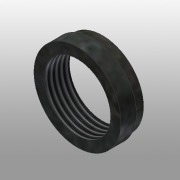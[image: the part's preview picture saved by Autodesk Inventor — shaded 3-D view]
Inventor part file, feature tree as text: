
AUTODESK INVENTOR PART (.ipt)
format: ipt  version: 2015 (Build 190159000, 159)  size: 107,520 bytes
history: native  units: mm
features: other x3, sketch x3
ambient origin geometry x8: Origin, YZ Plane, XZ Plane, XY Plane, X Axis, Y Axis, Z Axis, Center Point
bodies: Solid1 (feature_tree)
feature tree (6):
  other  "500-100.ipt"
  other  "Solid1::500-100.ipt"
  other  "TaggingFeature1"
  sketch  "Sketch1"  dims[d0=10.0mm]
  sketch  "Sketch2"
  sketch  "Sketch3"
